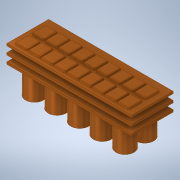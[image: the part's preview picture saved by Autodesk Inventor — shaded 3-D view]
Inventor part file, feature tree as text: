
AUTODESK INVENTOR PART (.ipt)
format: ipt  version: 2020 (Build 240168000, 168)  size: 684,032 bytes
history: native  units: mm
features: chamfer x16, extrude x9, sketch x9, other x2
ambient origin geometry x8: Origin, YZ Plane, XZ Plane, XY Plane, X Axis, Y Axis, Z Axis, Center Point
bodies: Body1 (feature_tree)
feature tree (36):
  other  "Bryła1"
  extrude  "Wyciągnięcie proste1"  Depth=18.73mm
  extrude  "Wyciągnięcie proste2"  Depth=9.365mm
  chamfer  "Faza1"  Distance=55.88mm
  chamfer  "Faza2"  Distance=27.94mm
  chamfer  "Faza3"  Distance=1.0mm
  extrude  "Wyciągnięcie proste3"  Depth=6.03mm
  chamfer  "Faza4"  Distance=5.08mm
  extrude  "Wyciągnięcie proste4"  Depth=2.54mm
  chamfer  "Faza5"  Distance=1.27mm
  chamfer  "Faza6"  Distance=5.08mm
  chamfer  "Faza7"  Distance=6.03mm
  chamfer  "Faza8"  Distance=1.27mm
  chamfer  "Faza9"  Distance=0.64mm
  chamfer  "Faza10"  Distance=5.08mm
  chamfer  "Faza11"  Distance=0.64mm
  chamfer  "Faza12"  Distance=5.08mm
  chamfer  "Faza13"  Distance=0.64mm
  chamfer  "Faza14"  Distance=5.08mm
  chamfer  "Faza15"  Distance=0.64mm
  chamfer  "Faza16"  Distance=5.08mm
  other  "Płaszczyzna konstrukcyjna1"
  extrude  "Wyciągnięcie proste5"  Depth=5.08mm
  extrude  "Wyciągnięcie proste6"  Depth=5.08mm
  extrude  "Wyciągnięcie proste7"  Depth=5.08mm
  extrude  "Wyciągnięcie proste8"  Depth=0.64mm
  extrude  "Wyciągnięcie proste9"  Depth=0.64mm
  sketch  "Szkic1"
  sketch  "Szkic2"
  sketch  "Szkic3"
  sketch  "Szkic4"
  sketch  "Szkic5"
  sketch  "Szkic6"
  sketch  "Szkic7"
  sketch  "Szkic8"
  sketch  "Szkic9"
